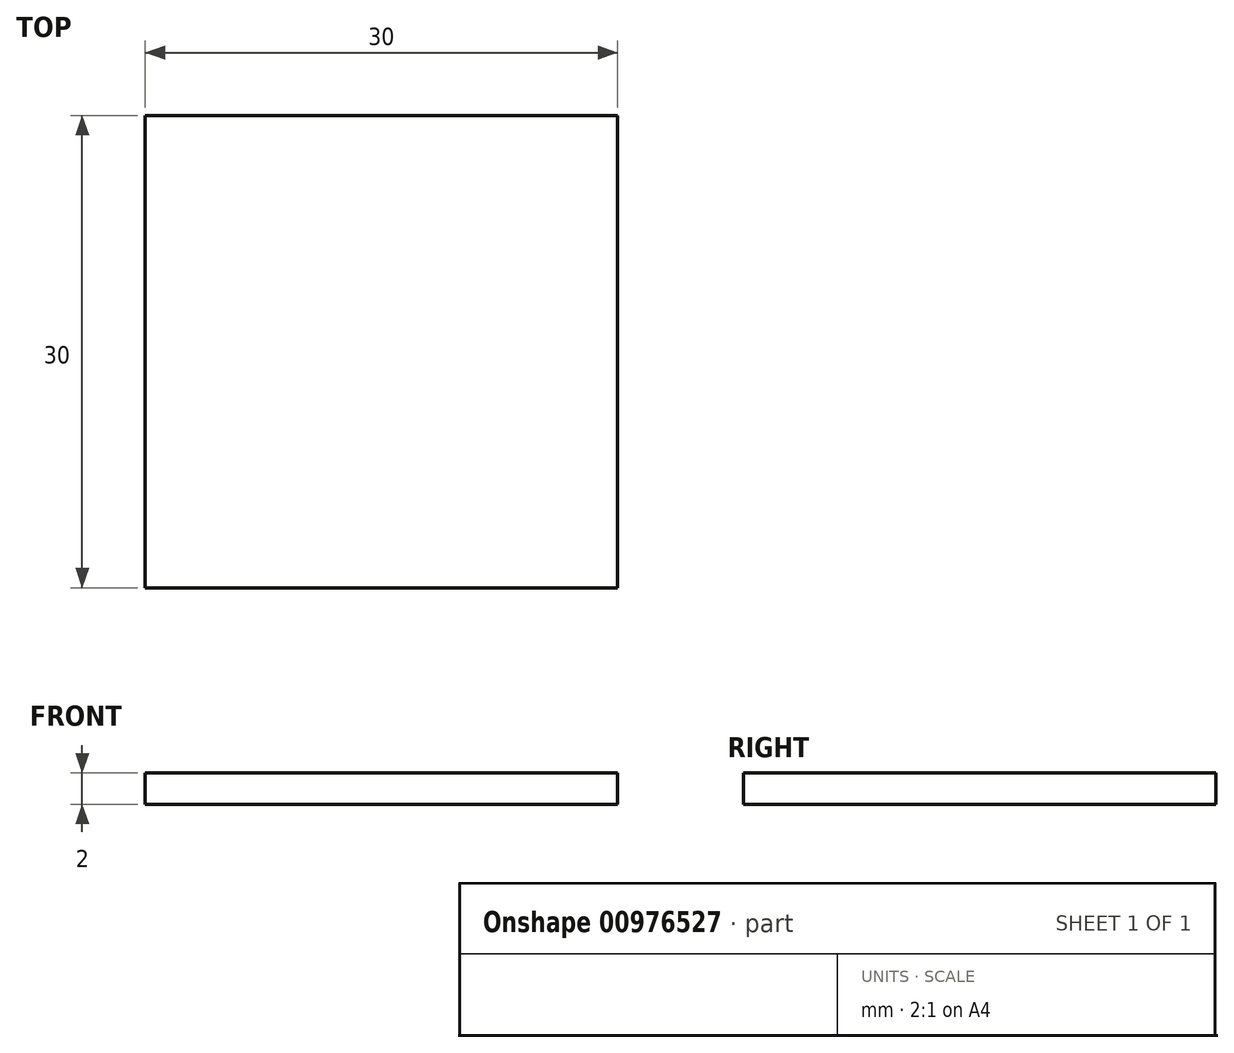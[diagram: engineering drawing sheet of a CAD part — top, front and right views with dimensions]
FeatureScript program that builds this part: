
annotation { "Feature Type Name" : "Feature", "Feature Type Description" : "" }
export const myFeature = defineFeature(function(context is Context, id is Id, definition is map)
    precondition{}
    {
        {
            var Q0;
            Q0=qCreatedBy(makeId("Top.planeOp"),FACE);
            var sketch = newSketch(context, id + "F0", { "sketchPlane" : qUnion([Q0])});
            skLineSegment(sketch, "E0.bottom", {"start": v(15, -15) * mm, "end": v(-15, -15) * mm});
            skLineSegment(sketch, "E0.top", {"start": v(15, 15) * mm, "end": v(-15, 15) * mm});
            skLineSegment(sketch, "E0.left", {"start": v(15, -15) * mm, "end": v(15, 15) * mm});
            skLineSegment(sketch, "E0.right", {"start": v(-15, -15) * mm, "end": v(-15, 15) * mm});
            skPoint(sketch, "E0.middle", {"position": v(0, 0) * mm});
            skSolve(sketch);
        }
        {
            var Q0;
            Q0 = qSketchRegion(id + "F0", true);
            extrude(context, id + "F1", {"entities" : qUnion([Q0]), "depth" : 2 * mm, "offsetDistance" : 25 * mm});
        }
    });
